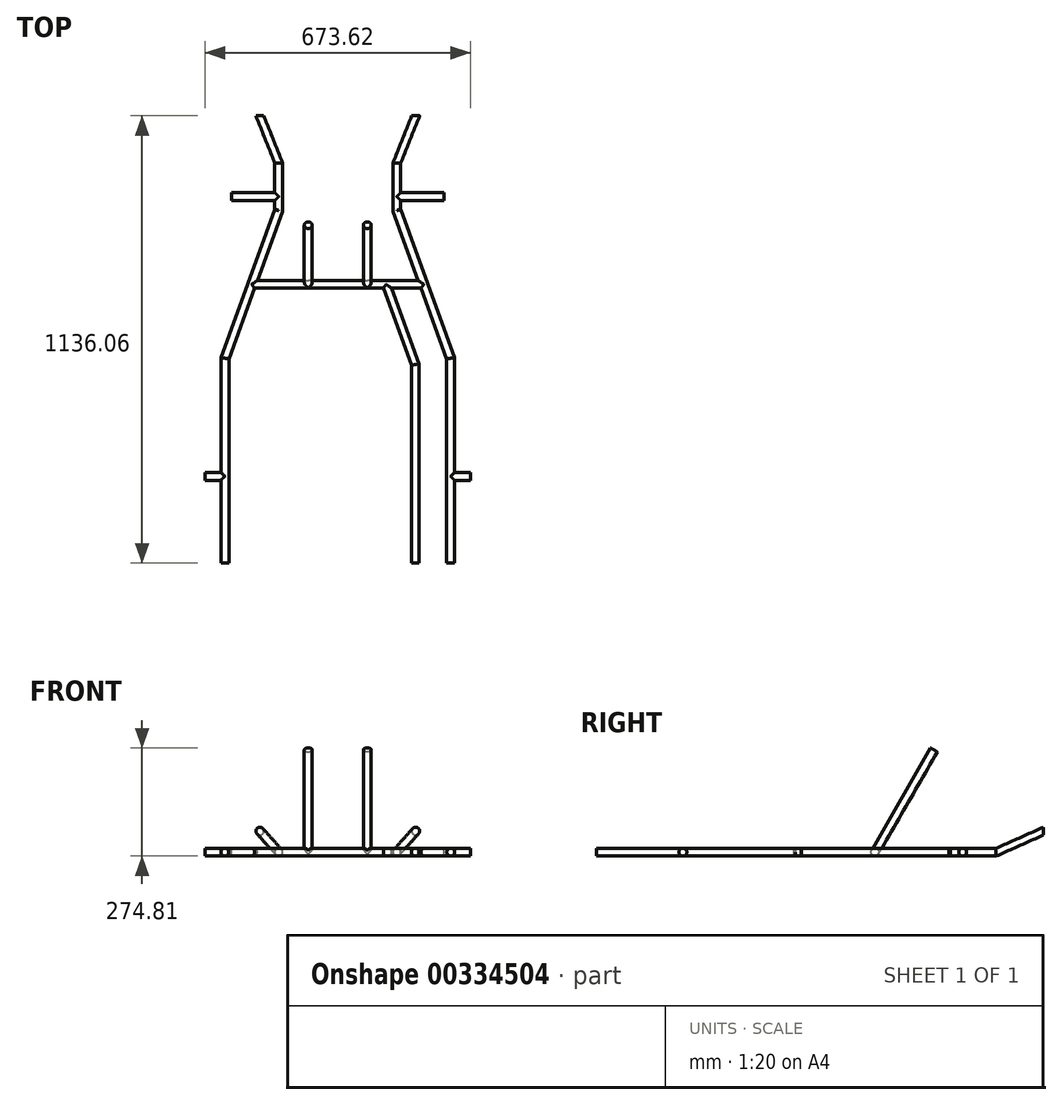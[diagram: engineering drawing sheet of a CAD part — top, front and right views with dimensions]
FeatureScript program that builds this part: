
annotation { "Feature Type Name" : "Feature", "Feature Type Description" : "" }
export const myFeature = defineFeature(function(context is Context, id is Id, definition is map)
    precondition{}
    {
        {
            var Q0;
            Q0=qCreatedBy(makeId("Top.planeOp"),FACE);
            var sketch = newSketch(context, id + "F0", { "sketchPlane" : qUnion([Q0])});
            skLineSegment(sketch, "E0", {"start": v(-150, 0) * mm, "end": v(-150, -120) * mm});
            skPoint(sketch, "E1.visualSharp", {"position": v(-150, -100) * mm});
            skLineSegment(sketch, "E2", {"start": v(-150, -120) * mm, "end": v(-286.8, -495.88) * mm});
            skLineSegment(sketch, "E3", {"start": v(-286.8, -495.88) * mm, "end": v(-286.8, -845.88) * mm});
            skLineSegment(sketch, "E4", {"start": v(-286.8, -795.88) * mm, "end": v(-336.8, -795.88) * mm});
            skLineSegment(sketch, "E5", {"start": v(-150, -85) * mm, "end": v(-270, -85) * mm});
            skLineSegment(sketch, "E6", {"start": v(-218.4, -307.94) * mm, "end": v(0, -307.94) * mm});
            skLineSegment(sketch, "E7", {"start": v(-286.8, -845.88) * mm, "end": v(-286.8, -1015.88) * mm});
            skSolve(sketch);
        }
        {
            var Q0;
            Q0=qCreatedBy(makeId("Front.planeOp"),FACE);
            var sketch = newSketch(context, id + "F1", { "sketchPlane" : qUnion([Q0])});
            skCircle(sketch, "E8", {"center": v(-150, 0) * mm, "radius": 10 * mm});
            skSolve(sketch);
        }
        {
            var Q0;
            Q0=makeQuery(id+"F1.imprint","IMPRINT",FACE,{"disambiguationData":[TD([[makeQuery(id+"F1.imprint","IMPRINT",EDGE,{"derivedFrom":sQuery(id+"F1.wireOp",EDGE,"E8")}),1.0]])]});
            var Q1;
            Q1=sQuery(id+"F1.wireOp",EDGE,"E8");
            var Q2;
            Q2=sQuery(id+"F0.wireOp",EDGE,"E2");
            var Q3;
            Q3=sQuery(id+"F0.wireOp",EDGE,"E0");
            var Q4;
            Q4=sQuery(id+"F0.wireOp",EDGE,"E3");
            var Q5;
            Q5=sQuery(id+"F0.wireOp",EDGE,"E7");
            sweep(context, id + "F2", {"profiles" : qUnion([Q0]), "surfaceProfiles" : qUnion([Q1]), "path" : qUnion([Q2, Q3, Q4, Q5])});
        }
        {
            var Q0;
            Q0=makeQuery(id+"F2.opSweep","MID_CAP_EDGE",EDGE,{"disambiguationData":[OSD([sQuery(id+"F0.wireOp",VERTEX,"E0.end"),sQuery(id+"F1.wireOp",EDGE,"E8")])],"capPos":1.0});
            fillet(context, id + "F3", {"entities" : qUnion([Q0]), "radius" : 10 * mm, "tangentPropagation" : true, "allowEdgeOverflow" : false});
        }
        {
            var Q0;
            Q0=qCreatedBy(makeId("Right.planeOp"),FACE);
            var Q1;
            Q1=sQuery(id+"F0.wireOp",VERTEX,"E4.end");
            cPlane(context, id + "F4", {"entities" : qUnion([Q0, Q1]), "cplaneType" : CPlaneType.PLANE_POINT, "offset" : 25 * mm, "width" : 150 * mm, "height" : 150 * mm});
        }
        {
            var Q0;
            Q0=qCreatedBy(id+"F4.planeOp",FACE);
            var sketch = newSketch(context, id + "F5", { "sketchPlane" : qUnion([Q0])});
            skCircle(sketch, "E9", {"center": v(-795.88, 0) * mm, "radius": 10 * mm});
            skSolve(sketch);
        }
        {
            var Q0;
            Q0=makeQuery(id+"F5.imprint","IMPRINT",FACE,{"disambiguationData":[TD([[makeQuery(id+"F5.imprint","IMPRINT",EDGE,{"derivedFrom":sQuery(id+"F5.wireOp",EDGE,"E9")}),1.0]])]});
            var Q1;
            Q1=sQuery(id+"F0.wireOp",EDGE,"E4");
            sweep(context, id + "F6", {"operationType" : NewBodyOperationType.ADD, "profiles" : qUnion([Q0]), "path" : qUnion([Q1])});
        }
        {
            var Q0;
            Q0=sQuery(id+"F0.wireOp",EDGE,"E0");
            cPoint(context, id + "F7", {"entities" : qUnion([Q0]), "parameter" : 0.5});
        }
        {
            var Q0;
            Q0=qCreatedBy(makeId("Right.planeOp"),FACE);
            var Q1;
            Q1=qCreatedBy(id+"F7",VERTEX);
            cPlane(context, id + "F8", {"entities" : qUnion([Q0, Q1]), "cplaneType" : CPlaneType.PLANE_POINT, "offset" : 25 * mm, "width" : 150 * mm, "height" : 150 * mm});
        }
        {
            var Q0;
            Q0=qCreatedBy(id+"F8.planeOp",FACE);
            var sketch = newSketch(context, id + "F9", { "sketchPlane" : qUnion([Q0])});
            skCircle(sketch, "E10", {"center": v(-85, 0) * mm, "radius": 10 * mm});
            skSolve(sketch);
        }
        {
            var Q0;
            Q0=qSketchRegion(id+"F9",true);
            var Q1;
            Q1=sQuery(id+"F0.wireOp",EDGE,"E5");
            sweep(context, id + "F10", {"operationType" : NewBodyOperationType.ADD, "profiles" : qUnion([Q0]), "path" : qUnion([Q1])});
        }
        {
            var Q0;
            Q0=qCreatedBy(makeId("Right.planeOp"),FACE);
            var sketch = newSketch(context, id + "F11", { "sketchPlane" : qUnion([Q0])});
            skCircle(sketch, "E11", {"center": v(-307.94, 0) * mm, "radius": 10 * mm});
            skSolve(sketch);
        }
        {
            var Q0;
            Q0=makeQuery(id+"F11.imprint","IMPRINT",FACE,{"disambiguationData":[TD([[makeQuery(id+"F11.imprint","IMPRINT",EDGE,{"derivedFrom":sQuery(id+"F11.wireOp",EDGE,"E11")}),1.0]])]});
            var Q1;
            Q1=sQuery(id+"F0.wireOp",EDGE,"E6");
            sweep(context, id + "F12", {"operationType" : NewBodyOperationType.ADD, "profiles" : qUnion([Q0]), "path" : qUnion([Q1])});
        }
        {
            var Q0;
            Q0=qCreatedBy(makeId("Top.planeOp"),FACE);
            var sketch = newSketch(context, id + "F13", { "sketchPlane" : qUnion([Q0])});
            skLineSegment(sketch, "E12", {"start": v(-74.15, 0) * mm, "end": v(73.31, 0) * mm, "construction": true});
            skSolve(sketch);
        }
        {
            var Q0;
            Q0=sQuery(id+"F13.wireOp",EDGE,"E12");
            var Q1;
            Q1=qCreatedBy(makeId("Top.planeOp"),FACE);
            cPlane(context, id + "F14", {"entities" : qUnion([Q0, Q1]), "cplaneType" : CPlaneType.LINE_ANGLE, "offset" : 25 * mm, "angle" : 24 * degree, "width" : 150 * mm, "height" : 150 * mm});
        }
        {
            var Q0;
            Q0=qCreatedBy(id+"F14.planeOp",FACE);
            var sketch = newSketch(context, id + "F15", { "sketchPlane" : qUnion([Q0])});
            skLineSegment(sketch, "E13", {"start": v(-150, 0) * mm, "end": v(-197.88, -131.56) * mm});
            skSolve(sketch);
        }
        {
            var Q0;
            Q0=makeQuery(id+"F2.opSweep","CAP_FACE",FACE,{"disambiguationData":[OSD([sQuery(id+"F0.wireOp",VERTEX,"E0.start"),sQuery(id+"F1.wireOp",EDGE,"E8")])],"isStart":true});
            var Q1;
            Q1=sQuery(id+"F15.wireOp",EDGE,"E13");
            sweep(context, id + "F16", {"operationType" : NewBodyOperationType.ADD, "profiles" : qUnion([Q0]), "path" : qUnion([Q1])});
        }
        {
            var Q0;
            Q0=makeQuery(id+"F2.opSweep","SWEPT_BODY",BODY,{"disambiguationData":[OSD([sQuery(id+"F0.wireOp",EDGE,"E0"),sQuery(id+"F1.wireOp",EDGE,"E8")])]});
            var Q1;
            Q1=qCreatedBy(makeId("Right.planeOp"),FACE);
            mirror(context, id + "F17", {"operationType" : NewBodyOperationType.ADD, "entities" : qUnion([Q0]), "mirrorPlane" : qUnion([Q1])});
        }
        {
            var Q0;
            Q0=qCreatedBy(makeId("Top.planeOp"),FACE);
            var sketch = newSketch(context, id + "F18", { "sketchPlane" : qUnion([Q0])});
            skLineSegment(sketch, "E14", {"start": v(196.8, -511.75) * mm, "end": v(196.8, -1015.88) * mm});
            skLineSegment(sketch, "E15", {"start": v(342.92, -1015.88) * mm, "end": v(-44.03, -1015.88) * mm, "construction": true});
            skLineSegment(sketch, "E16", {"start": v(286.8, -394.8) * mm, "end": v(286.8, -1101.3) * mm, "construction": true});
            skLineSegment(sketch, "E17", {"start": v(196.8, -511.75) * mm, "end": v(122.63, -307.94) * mm});
            skLineSegment(sketch, "E18", {"start": v(0, -307.94) * mm, "end": v(185.84, -307.94) * mm, "construction": true});
            skPoint(sketch, "E19", {"position": v(92.92, -307.94) * mm});
            skLineSegment(sketch, "E20", {"start": v(286.8, -495.88) * mm, "end": v(219, -309.57) * mm, "construction": true});
            skSolve(sketch);
        }
        {
            var Q0;
            Q0=qCreatedBy(makeId("Front.planeOp"),FACE);
            var Q1;
            Q1=sQuery(id+"F18.wireOp",VERTEX,"E14.end");
            cPlane(context, id + "F19", {"entities" : qUnion([Q0, Q1]), "cplaneType" : CPlaneType.PLANE_POINT, "offset" : 25 * mm, "width" : 150 * mm, "height" : 150 * mm});
        }
        {
            var Q0;
            Q0=qCreatedBy(id+"F19.planeOp",FACE);
            var sketch = newSketch(context, id + "F20", { "sketchPlane" : qUnion([Q0])});
            skCircle(sketch, "E21", {"center": v(196.8, 0) * mm, "radius": 10 * mm});
            skSolve(sketch);
        }
        {
            var Q0;
            Q0=makeQuery(id+"F20.imprint","IMPRINT",FACE,{"disambiguationData":[TD([[makeQuery(id+"F20.imprint","IMPRINT",EDGE,{"derivedFrom":sQuery(id+"F20.wireOp",EDGE,"E21")}),1.0]])]});
            var Q1;
            Q1=sQuery(id+"F18.wireOp",EDGE,"E14");
            var Q2;
            Q2=sQuery(id+"F18.wireOp",EDGE,"E17");
            sweep(context, id + "F21", {"operationType" : NewBodyOperationType.ADD, "profiles" : qUnion([Q0]), "path" : qUnion([Q1, Q2])});
        }
        {
            var Q0;
            Q0=sQuery(id+"F0.wireOp",EDGE,"E6");
            cPlane(context, id + "F22", {"entities" : qUnion([Q0]), "cplaneType" : CPlaneType.LINE_ANGLE, "offset" : 25 * mm, "angle" : 150 * degree, "width" : 150 * mm, "height" : 150 * mm});
        }
        {
            var Q0;
            Q0=qCreatedBy(id+"F22.planeOp",FACE);
            var sketch = newSketch(context, id + "F23", { "sketchPlane" : qUnion([Q0])});
            skLineSegment(sketch, "E22", {"start": v(0, -153.97) * mm, "end": v(0, -100.6) * mm, "construction": true});
            skLineSegment(sketch, "E23", {"start": v(-75, -143.97) * mm, "end": v(-75, 156.03) * mm});
            skSolve(sketch);
        }
        {
            var Q0;
            Q0=sQuery(id+"F0.wireOp",EDGE,"E6");
            cPlane(context, id + "F24", {"entities" : qUnion([Q0]), "cplaneType" : CPlaneType.LINE_ANGLE, "offset" : 25 * mm, "angle" : 240 * degree, "width" : 150 * mm, "height" : 150 * mm});
        }
        {
            var Q0;
            Q0=qCreatedBy(id+"F24.planeOp",FACE);
            cPlane(context, id + "F25", {"entities" : qUnion([Q0]), "cplaneType" : CPlaneType.OFFSET, "offset" : 0 * mm, "width" : 150 * mm, "height" : 150 * mm});
        }
        {
            var Q0;
            Q0=qCreatedBy(id+"F25.planeOp",FACE);
            var sketch = newSketch(context, id + "F26", { "sketchPlane" : qUnion([Q0])});
            skCircle(sketch, "E24", {"center": v(-75, 266.68) * mm, "radius": 10 * mm});
            skSolve(sketch);
        }
        {
            var Q0;
            Q0=makeQuery(id+"F26.imprint","IMPRINT",FACE,{"disambiguationData":[TD([[makeQuery(id+"F26.imprint","IMPRINT",EDGE,{"derivedFrom":sQuery(id+"F26.wireOp",EDGE,"E24")}),1.0]])]});
            var Q1;
            Q1=sQuery(id+"F23.wireOp",EDGE,"E23");
            sweep(context, id + "F27", {"profiles" : qUnion([Q0]), "path" : qUnion([Q1])});
        }
        {
            var Q0;
            Q0=makeQuery(id+"F27.opSweep","SWEPT_BODY",BODY,{"disambiguationData":[OSD([sQuery(id+"F23.wireOp",EDGE,"E23"),sQuery(id+"F26.wireOp",EDGE,"E24")])]});
            var Q1;
            Q1=qCreatedBy(makeId("Right.planeOp"),FACE);
            mirror(context, id + "F28", {"operationType" : NewBodyOperationType.ADD, "entities" : qUnion([Q0]), "mirrorPlane" : qUnion([Q1])});
        }
    });
